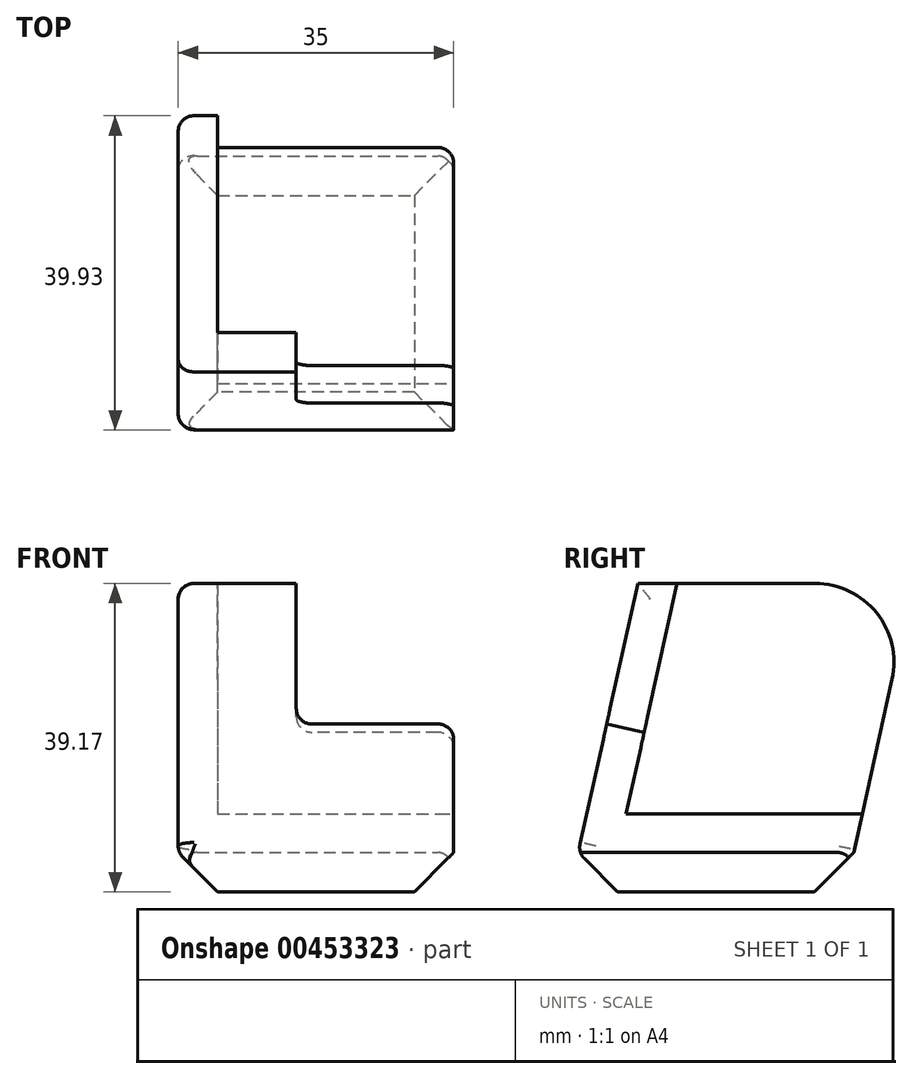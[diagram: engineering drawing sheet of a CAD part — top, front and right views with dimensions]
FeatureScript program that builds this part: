
annotation { "Feature Type Name" : "Feature", "Feature Type Description" : "" }
export const myFeature = defineFeature(function(context is Context, id is Id, definition is map)
    precondition{}
    {
        {
            var Q0;
            Q0=qCreatedBy(makeId("Right.planeOp"),FACE);
            var sketch = newSketch(context, id + "F0", { "sketchPlane" : qUnion([Q0])});
            skLineSegment(sketch, "E0", {"start": v(0, 0) * mm, "end": v(7.58, 34.17) * mm});
            skLineSegment(sketch, "E1", {"start": v(7.58, 34.17) * mm, "end": v(42.58, 34.17) * mm});
            skLineSegment(sketch, "E2", {"start": v(42.58, 34.17) * mm, "end": v(35, 0) * mm});
            skLineSegment(sketch, "E3", {"start": v(35, 0) * mm, "end": v(0, 0) * mm});
            skSolve(sketch);
        }
        {
            var Q0;
            Q0=makeQuery(id+"F0.imprint","IMPRINT",FACE,{"disambiguationData":[TD([[makeQuery(id+"F0.imprint","IMPRINT",EDGE,{"derivedFrom":sQuery(id+"F0.wireOp",EDGE,"E0")}),-1.0]])]});
            extrude(context, id + "F1", {"entities" : qUnion([Q0]), "oppositeDirection" : true, "depth" : 35 * mm});
        }
        {
            var Q0;
            Q0=makeQuery(id+"F1.opExtrude","CAP_FACE",FACE,{"disambiguationData":[OSD([sQuery(id+"F0.wireOp",EDGE,"E0"),sQuery(id+"F0.wireOp",EDGE,"E1"),sQuery(id+"F0.wireOp",EDGE,"E2"),sQuery(id+"F0.wireOp",EDGE,"E3")])],"isStart":true});
            var sketch = newSketch(context, id + "F2", { "sketchPlane" : qUnion([Q0])});
            skLineSegment(sketch, "E4", {"start": v(12.58, 34.17) * mm, "end": v(6.08, 4.88) * mm});
            skLineSegment(sketch, "E5", {"start": v(6.08, 4.88) * mm, "end": v(36.08, 4.88) * mm});
            skLineSegment(sketch, "E6", {"start": v(36.08, 4.88) * mm, "end": v(42.58, 34.17) * mm});
            skLineSegment(sketch, "E7", {"start": v(42.58, 34.17) * mm, "end": v(12.58, 34.17) * mm});
            skSolve(sketch);
        }
        {
            var Q0;
            Q0=makeQuery(id+"F2.imprint","IMPRINT",FACE,{"disambiguationData":[TD([[makeQuery(id+"F2.imprint","IMPRINT",EDGE,{"derivedFrom":sQuery(id+"F2.wireOp",EDGE,"E4")}),1.0]])]});
            extrude(context, id + "F3", {"entities" : qUnion([Q0]), "operationType" : NewBodyOperationType.REMOVE, "oppositeDirection" : true, "depth" : 30 * mm});
        }
        {
            var Q0;
            Q0=makeQuery(id+"F1.opExtrude","SWEPT_FACE",FACE,{"disambiguationData":[OSD([sQuery(id+"F0.wireOp",EDGE,"E0")])]});
            var sketch = newSketch(context, id + "F4", { "sketchPlane" : qUnion([Q0])});
            skLineSegment(sketch, "E8.bottom", {"start": v(0, 35) * mm, "end": v(-20, 35) * mm});
            skLineSegment(sketch, "E8.top", {"start": v(0, 16.72) * mm, "end": v(-20, 16.72) * mm});
            skLineSegment(sketch, "E8.left", {"start": v(0, 35) * mm, "end": v(0, 16.72) * mm});
            skLineSegment(sketch, "E8.right", {"start": v(-20, 35) * mm, "end": v(-20, 16.72) * mm});
            skSolve(sketch);
        }
        {
            var Q0;
            Q0=makeQuery(id+"F4.imprint","IMPRINT",FACE,{"disambiguationData":[TD([[makeQuery(id+"F4.imprint","IMPRINT",EDGE,{"derivedFrom":sQuery(id+"F4.wireOp",EDGE,"E8.bottom")}),-1.0]])]});
            extrude(context, id + "F5", {"entities" : qUnion([Q0]), "operationType" : NewBodyOperationType.REMOVE, "endBound" : BoundingType.THROUGH_ALL, "oppositeDirection" : true, "depth" : 25 * mm});
        }
        {
            var Q0;
            Q0=makeQuery(id+"F1.opExtrude","SWEPT_FACE",FACE,{"disambiguationData":[OSD([sQuery(id+"F0.wireOp",EDGE,"E1")])]});
            var sketch = newSketch(context, id + "F6", { "sketchPlane" : qUnion([Q0])});
            skLineSegment(sketch, "E9", {"start": v(-20, 7.58) * mm, "end": v(-20, 12.58) * mm});
            skSolve(sketch);
        }
        {
            var Q0;
            {var subQ0=sQuery(id+"F6.wireOp",EDGE,"E9");Q0=makeQuery(id+"F6.imprint","IMPRINT",FACE,{"disambiguationData":[TD([[makeQuery(id+"F6.imprint","IMPRINT",EDGE,{"derivedFrom":subQ0}),-1.0]])]});}
            extrude(context, id + "F7", {"entities" : qUnion([Q0]), "operationType" : NewBodyOperationType.REMOVE, "oppositeDirection" : true, "depth" : 5 * mm});
        }
        {
            var Q0;
            Q0=makeQuery(id+"F1.opExtrude","SWEPT_FACE",FACE,{"disambiguationData":[OSD([sQuery(id+"F0.wireOp",EDGE,"E3")])]});
            extrude(context, id + "F8", {"entities" : qUnion([Q0]), "operationType" : NewBodyOperationType.ADD, "depth" : 5 * mm});
        }
        {
            var Q0;
            Q0=makeQuery(id+"F8.opExtrude","CAP_FACE",FACE,{"disambiguationData":[OSD([sQuery(id+"F0.wireOp",EDGE,"E3")])],"isStart":false});
            chamfer(context, id + "F9", {"entities" : qUnion([Q0]), "width" : 5 * mm, "tangentPropagation" : true});
        }
        {
            var Q0;
            Q0=makeQuery(id+"F1.opExtrude","CAP_EDGE",EDGE,{"disambiguationData":[OSD([sQuery(id+"F0.wireOp",EDGE,"E1")])],"isStart":false});
            var Q1;
            Q1=makeQuery(id+"F7.boolean.opBoolean","COPY",EDGE,{"derivedFrom":makeQuery(id+"F7.opExtrude","CAP_EDGE",EDGE,{"disambiguationData":[OSD([sQuery(id+"F6.wireOp",EDGE,"E9")])],"isStart":true})});
            var Q2;
            Q2=makeQuery(id+"F5.boolean.opBoolean","COPY",EDGE,{"derivedFrom":makeQuery(id+"F5.opExtrude","SWEPT_EDGE",EDGE,{"disambiguationData":[OSD([sQuery(id+"F4.wireOp",EDGE,"E8.top"),sQuery(id+"F4.wireOp",EDGE,"E8.right")])]})});
            var Q3;
            Q3=makeQuery(id+"F5.boolean.opBoolean","COPY",EDGE,{"derivedFrom":makeQuery(id+"F5.opExtrude","SWEPT_EDGE",EDGE,{"disambiguationData":[OSD([sQuery(id+"F0.wireOp",EDGE,"E0"),sQuery(id+"F4.wireOp",EDGE,"E8.top"),sQuery(id+"F4.wireOp",EDGE,"E8.left")])]})});
            var Q4;
            Q4=makeQuery(id+"F1.opExtrude","CAP_EDGE",EDGE,{"disambiguationData":[OSD([sQuery(id+"F0.wireOp",EDGE,"E0")])],"isStart":false});
            var Q5;
            Q5=makeQuery(id+"F1.opExtrude","CAP_EDGE",EDGE,{"disambiguationData":[OSD([sQuery(id+"F0.wireOp",EDGE,"E2")])],"isStart":false});
            var Q6;
            {var subQ0=sQuery(id+"F0.wireOp",EDGE,"E0");Q6=makeQuery(id+"F9.opChamfer","BLEND_EDGE",EDGE,{"blendedFrom":[makeQuery(id+"F8.opExtrude","CAP_EDGE",EDGE,{"disambiguationData":[OSD([subQ0,sQuery(id+"F0.wireOp",EDGE,"E3")])],"isStart":false}),makeQuery(id+"F1.opExtrude","SWEPT_FACE",FACE,{"disambiguationData":[OSD([subQ0])]})],"blendedInto":[makeQuery(id+"F1.opExtrude","SWEPT_FACE",FACE,{"disambiguationData":[OSD([subQ0])]})]});}
            fillet(context, id + "F10", {"entities" : qUnion([Q0, Q1, Q2, Q3, Q4, Q5, Q6]), "radius" : 2 * mm, "tangentPropagation" : true, "allowEdgeOverflow" : false});
        }
        {
            var Q0;
            Q0=makeQuery(id+"F1.opExtrude","CAP_EDGE",EDGE,{"disambiguationData":[OSD([sQuery(id+"F0.wireOp",EDGE,"E2")])],"isStart":true});
            fillet(context, id + "F11", {"entities" : qUnion([Q0]), "radius" : 2 * mm, "tangentPropagation" : true, "allowEdgeOverflow" : false});
        }
        {
            var Q0;
            {var subQ0=sQuery(id+"F0.wireOp",EDGE,"E3");var subQ1=makeQuery(id+"F1.opExtrude","CAP_EDGE",EDGE,{"disambiguationData":[OSD([subQ0])],"isStart":false});Q0=makeQuery(id+"F9.opChamfer","BLEND_EDGE",EDGE,{"blendedFrom":[makeQuery(id+"F8.opExtrude","CAP_EDGE",EDGE,{"disambiguationData":[OSD([subQ0]),TDD([subQ1])],"isStart":false}),makeQuery(id+"F8.boolean.opBoolean","MERGE",FACE,{"derivedFrom":[makeQuery(id+"F1.opExtrude","CAP_FACE",FACE,{"disambiguationData":[OSD([sQuery(id+"F0.wireOp",EDGE,"E0"),sQuery(id+"F0.wireOp",EDGE,"E1"),sQuery(id+"F0.wireOp",EDGE,"E2"),subQ0])],"isStart":false}),makeQuery(id+"F8.opExtrude","SWEPT_FACE",FACE,{"disambiguationData":[OSD([subQ0]),TDD([subQ1])]})]})],"blendedInto":[makeQuery(id+"F8.boolean.opBoolean","MERGE",FACE,{"derivedFrom":[makeQuery(id+"F1.opExtrude","CAP_FACE",FACE,{"disambiguationData":[OSD([sQuery(id+"F0.wireOp",EDGE,"E0"),sQuery(id+"F0.wireOp",EDGE,"E1"),sQuery(id+"F0.wireOp",EDGE,"E2"),subQ0])],"isStart":false}),makeQuery(id+"F8.opExtrude","SWEPT_FACE",FACE,{"disambiguationData":[OSD([subQ0]),TDD([subQ1])]})]})]});}
            fillet(context, id + "F12", {"entities" : qUnion([Q0]), "radius" : 2 * mm, "tangentPropagation" : true, "allowEdgeOverflow" : false});
        }
        {
            var Q0;
            Q0=makeQuery(id+"F1.opExtrude","SWEPT_EDGE",EDGE,{"disambiguationData":[OSD([sQuery(id+"F0.wireOp",EDGE,"E1"),sQuery(id+"F0.wireOp",EDGE,"E2")])]});
            fillet(context, id + "F13", {"entities" : qUnion([Q0]), "radius" : 10 * mm, "tangentPropagation" : true, "allowEdgeOverflow" : false});
        }
    });
